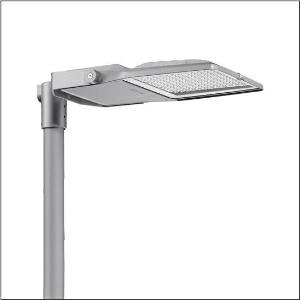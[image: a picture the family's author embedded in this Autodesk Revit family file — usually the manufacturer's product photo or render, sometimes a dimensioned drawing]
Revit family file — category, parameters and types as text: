
# Revit family: floodlight_fl_21_iq_midi___pl43_5xa7781f4a3a_cde7
name_source: partatom
category: Lighting Fixtures
units: mm (PartAtom-declared; Revit-internal decimal feet)

## family parameters
Cut with Voids When Loaded = No
Host = Face
Light Source = No
Part Type = Normal
Room Calculation Point = No
Round Connector Dimension = Use Diameter
Shared = No

## types (1)
- --- (1 x LED, 38290 lm, 270.2 W, 4000K)
    Apparent Load = 270 VA
    CIE Flux Codes = 27 78 99 100 100
    Color Rendering = 70
    Color Temperature = 4000K
    Default Elevation = 1800 mm
    Description = Floodlight FL 21 iQ midi, floodlight, primary light control with lens, of PMMA, primary optical cover: protective disc, of toughened safety glass, transparent, light distribution: PL43, light emission: direct distribution, installation type: surface-mounted, LED, High Power LED, rated luminous flux: 38.290lm, luminous efficacy: 142lm/W, light colour: 740, colour temperature: 4000K, control gear: ECG iQ, control: optimised constant luminous flux control (CLO 2.0), Desk-Remote (wireless, voltage-free reading and setting of iQ features in the workshop via application-optimized NFC function/RFID function), Light-Fading, Smart-Wire, Night-Set, Lumen-Switch, Temp-Guard, Auto-Match, with terminal, 6-pole, mains connection: 220..240V, AC, 50/60Hz, start of lifetime: 270W, end of service life: 287W, reduction: 118W, luminaire housing, of diecast aluminium, powder-coated, Siteco® metallic grey (DB 702S), corrosivity category C5 mid according to DIN EN ISO 12944, sealing non-destructively replaceable, please order mast flange separately, mast bracket, of steel, galvanised, powder-coated, Siteco® metallic grey (DB 702S), protection rating (complete): IP66, insulation class (complete): insulation class II (safety insulation), certification: CE, ENEC, VDE, protection symbol: D, impact resistance: IK08, permissible operating ambient temperature: -40..+40°C, permissible operating ambient temperature for outdoor applications: -40..+50°C, standard: DIN EN 12944, LABS conformity tested according to VDMA 24364:2018-05, packaging unit: 1 piece

Light Distribution: PL43
    Height = 76 mm
    Lamp = 1 x LED
    Lamp Light Flux = 38290 lm
    Lamp Power = 270.2 W
    Lamp count = 1
    Length = 657 mm
    Luminous efficacy = 142 lm/W
    Manufacturer = Siteco
    ModVariant = No
    Model = 5XA7781F4A3A
    Number of Poles = 1
    OnlyDefault = Yes
    Power Factor = 1
    Product Name = Floodlight FL 21 iQ midi | PL43
    Product group = floodlight | pylon annexe
    ProductGroupID = 6200
    Protection Class = Protection class II
    Protection Degree = IP 66
    RLX_Detail_Level = 1
    RLX_Emergency_Light_Flux = 0 lm
    RLX_Emergency_Type = 0
    RLX_Emergency_Type_DB = No
    RlxData = <blob elided: 153609 chars, md5=5a97045a>
    Socket = socket
    Standby Power = 0 W
    System Light Flux = 38290 lm
    System Power = 270 W
    Type Comments = factory setting: luminous flux: 100 % | dim-lin: 254 | 620 mA
    Type Image = l_1007123.jpg
    URL = http://relux.com
    VarID = @adj_073659
    Voltage = 0 V
    Weight = 0.00 kg
    Width = 442 mm

## geometry (parser evidence)
native form markers: Blend x4, Sweep x15
no freeform markers — native parametric forms only
